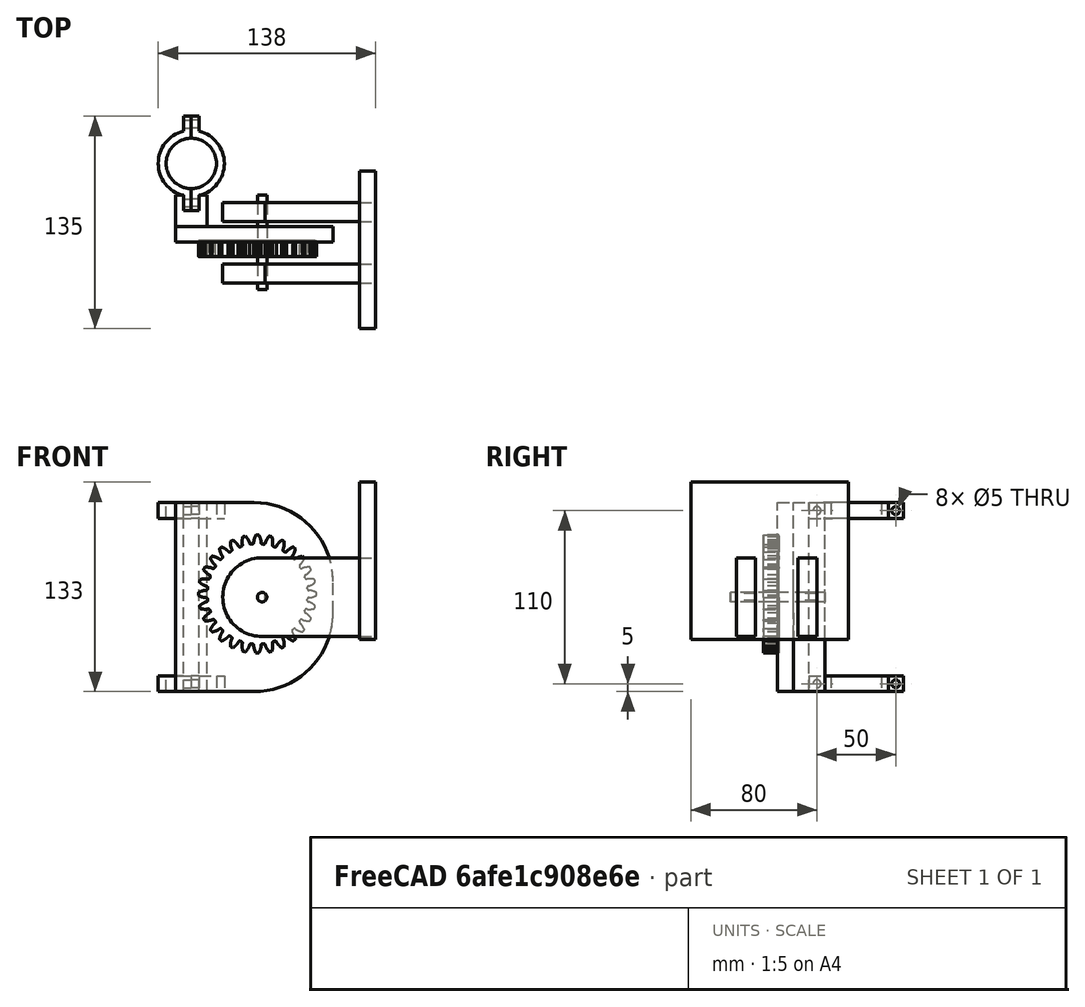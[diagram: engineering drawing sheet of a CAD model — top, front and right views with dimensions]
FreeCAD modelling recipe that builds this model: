
FCSTD DOCUMENT  (FreeCAD 0.18R4 (GitTag))
Label: Rotor_Z
License: All rights reserved
LicenseURL: http://en.wikipedia.org/wiki/All_rights_reserved
objects: Part::Cylinder×25, Part::Cut×19, Part::Box×14, Part::MultiFuse×6, Part::Fuse×4, Part::Fillet×2, Part::Part2DObjectPython×1, Part::Extrusion×1
note: 72 computed .brp shape members not serialized (recipe doc carries the construction recipe); baked Part::Feature solids carry a one-line shape summary decoded from their .brp

FEATURE [Part::Box] Box  label="Cubo"
  AttacherType = Attacher::AttachEngine3D
  Height = 10
  Length = 10
  Placement = pos=(-5,-30,0) rot=(0,0,1;0rad)
  Width = 60
FEATURE [Part::Box] Box001  label="Cubo001"
  AttacherType = Attacher::AttachEngine3D
  Height = 10
  Length = 21
  Placement = pos=(0,-30,0) rot=(0,0,1;0rad)
  Width = 60
FEATURE [Part::Cylinder] Cylinder  label="Cilindro"
  Angle = 360
  AttacherType = Attacher::AttachEngine3D
  Height = 10
  Placement = pos=(-5,-25,5) rot=(0,1,0;1.5708rad)
  Radius = 2.5
FEATURE [Part::Cylinder] Cylinder003  label="Cilindro001"
  Angle = 360
  AttacherType = Attacher::AttachEngine3D
  Height = 10
  Placement = pos=(-5,25,5) rot=(0,1,0;1.5708rad)
  Radius = 2.5
FEATURE [Part::MultiFuse] Fusion001  label="Agug"
  Shapes = -> [Cylinder,Cylinder003]
FEATURE [Part::Box] Box012  label="Cubo012"
  AttacherType = Attacher::AttachEngine3D
  Height = 120
  Length = 10
  Placement = pos=(-5,-45,0) rot=(0,0,1;0rad)
  Width = 10
FEATURE [Part::Box] Box013  label="Cubo013"
  AttacherType = Attacher::AttachEngine3D
  Height = 120
  Length = 20
  Placement = pos=(-10,-55,0) rot=(0,0,1;0rad)
  Width = 20
FEATURE [Part::Box] Box014  label="Cubo014"
  AttacherType = Attacher::AttachEngine3D
  Height = 120
  Length = 100
  Placement = pos=(-10,-46,0) rot=(0,0,1;0rad)
  Width = 10
FEATURE [Part::Part2DObjectPython] InvoluteGear  # Draft 2D object (typed FeaturePython)
  ExternalGear = true
  HighPrecision = true
  Modules = 2.5
  NumberOfTeeth = 28
  PressureAngle = 20
FEATURE [Part::Extrusion] Extrude
  Base = -> InvoluteGear
  Dir = (0,0,1)
  DirMode = 2
  FaceMakerClass = Part::FaceMakerBullseye
  LengthFwd = 10
  LengthRev = 0
  Placement = pos=(42,-45,62) rot=(1,0,0;1.5708rad)
  Solid = true
  Symmetric = false
FEATURE [Part::Box] Box015  label="Cubo015"
  AttacherType = Attacher::AttachEngine3D
  Height = 12
  Length = 70
  Placement = pos=(31,-70,-13) rot=(0,0,1;0rad)
  Width = 50
FEATURE [Part::Cylinder] Cylinder016  label="Cilindro008"
  Angle = 360
  AttacherType = Attacher::AttachEngine3D
  Height = 12
  Placement = pos=(29,-45,-13) rot=(0,0,1;0rad)
  Radius = 25
FEATURE [Part::Cylinder] Cylinder017  label="Cilindro009"
  Angle = 360
  AttacherType = Attacher::AttachEngine3D
  Height = 12
  Placement = pos=(29,-45,-13) rot=(0,0,1;0rad)
  Radius = 3
FEATURE [Part::Cut] Cut017
  Base = -> Cylinder016
  Tool = -> Cylinder017
FEATURE [Part::MultiFuse] Fusion008  label="lateral"
  Placement = pos=(16,-34,105) rot=(1,0,0;1.5708rad)
  Shapes = -> [Box015,Cut017]
FEATURE [Part::Box] Box016  label="Cubo016"
  AttacherType = Attacher::AttachEngine3D
  Height = 12
  Length = 70
  Placement = pos=(31,-70,-13) rot=(0,0,1;0rad)
  Width = 50
FEATURE [Part::Cylinder] Cylinder018  label="Cilindro010"
  Angle = 360
  AttacherType = Attacher::AttachEngine3D
  Height = 12
  Placement = pos=(29,-45,-13) rot=(0,0,1;0rad)
  Radius = 25
FEATURE [Part::Cylinder] Cylinder019  label="Cilindro011"
  Angle = 360
  AttacherType = Attacher::AttachEngine3D
  Height = 12
  Placement = pos=(29,-45,-13) rot=(0,0,1;0rad)
  Radius = 3
FEATURE [Part::Cut] Cut018
  Base = -> Cylinder018
  Tool = -> Cylinder019
FEATURE [Part::MultiFuse] Fusion009  label="lateral001"
  Placement = pos=(16,-73,105) rot=(1,0,0;1.5708rad)
  Shapes = -> [Box016,Cut018]
FEATURE [Part::Box] Box017  label="Cubo017"
  AttacherType = Attacher::AttachEngine3D
  Height = 100
  Length = 10
  Placement = pos=(107,-101,33) rot=(0,0,1;0rad)
  Width = 100
FEATURE [Part::Cylinder] Cylinder020  label="Cilindro012"
  Angle = 360
  AttacherType = Attacher::AttachEngine3D
  Height = 60
  Placement = pos=(45,-16,60) rot=(1,0,0;1.5708rad)
  Radius = 3
FEATURE [Part::Fillet] Fillet
  Base = -> Box014
  Edges = 1 edges r=50: [Edge8]
FEATURE [Part::Fillet] Fillet001
  Base = -> Fillet
  Edges = 1 edges r=50: [Edge3]
FEATURE [Part::Cylinder] Cylinder021  label="Cilindro 32"
  Angle = 360
  AttacherType = Attacher::AttachEngine3D
  Height = 10
  Radius = 16
FEATURE [Part::Cylinder] Cylinder022  label="Cilindro42"
  Angle = 360
  AttacherType = Attacher::AttachEngine3D
  Height = 10
  Radius = 21
FEATURE [Part::Cut] Cut019
  Base = -> Cylinder022
  Tool = -> Cylinder021
FEATURE [Part::Fuse] Fusion
  Base = -> Box
  Tool = -> Cut019
FEATURE [Part::Cut] Cut
  Base = -> Fusion
  Tool = -> Fusion001
FEATURE [Part::Cut] Cut020
  Base = -> Cut
  Tool = -> Box001
FEATURE [Part::Cylinder] Cylinder023  label="Cilindro013"
  Angle = 360
  AttacherType = Attacher::AttachEngine3D
  Height = 10
  Radius = 16
FEATURE [Part::Cut] Cut021  label="Brida"
  Base = -> Cut020
  Placement = pos=(0,4,10) rot=(0,1,0;3.14159rad)
  Tool = -> Cylinder023
FEATURE [Part::Cylinder] Cylinder024  label="Cilindro014"
  Angle = 360
  AttacherType = Attacher::AttachEngine3D
  Height = 10
  Placement = pos=(-5,25,5) rot=(0,1,0;1.5708rad)
  Radius = 2.5
FEATURE [Part::Box] Box018  label="Cubo018"
  AttacherType = Attacher::AttachEngine3D
  Height = 10
  Length = 10
  Placement = pos=(-5,-30,0) rot=(0,0,1;0rad)
  Width = 60
FEATURE [Part::Cylinder] Cylinder025  label="Cilindro015"
  Angle = 360
  AttacherType = Attacher::AttachEngine3D
  Height = 10
  Placement = pos=(-5,-25,5) rot=(0,1,0;1.5708rad)
  Radius = 2.5
FEATURE [Part::Box] Box019  label="Cubo019"
  AttacherType = Attacher::AttachEngine3D
  Height = 10
  Length = 21
  Placement = pos=(0,-30,0) rot=(0,0,1;0rad)
  Width = 60
FEATURE [Part::MultiFuse] Fusion010  label="Agug001"
  Shapes = -> [Cylinder025,Cylinder024]
FEATURE [Part::Cylinder] Cylinder026  label="Cilindro 033"
  Angle = 360
  AttacherType = Attacher::AttachEngine3D
  Height = 10
  Radius = 16
FEATURE [Part::Cylinder] Cylinder027  label="Cilindro016"
  Angle = 360
  AttacherType = Attacher::AttachEngine3D
  Height = 10
  Radius = 21
FEATURE [Part::Cut] Cut024
  Base = -> Cylinder027
  Tool = -> Cylinder026
FEATURE [Part::Fuse] Fusion011
  Base = -> Box018
  Tool = -> Cut024
FEATURE [Part::Cut] Cut025
  Base = -> Fusion011
  Tool = -> Fusion010
FEATURE [Part::Cut] Cut022
  Base = -> Cut025
  Tool = -> Box019
FEATURE [Part::Cylinder] Cylinder028  label="Cilindro017"
  Angle = 360
  AttacherType = Attacher::AttachEngine3D
  Height = 10
  Radius = 16
FEATURE [Part::Cut] Cut023  label="Brida001"
  Base = -> Cut022
  Placement = pos=(0,4,0) rot=(0,0,1;0rad)
  Tool = -> Cylinder028
FEATURE [Part::Cylinder] Cylinder029  label="Cilindro018"
  Angle = 360
  AttacherType = Attacher::AttachEngine3D
  Height = 10
  Placement = pos=(-5,25,5) rot=(0,1,0;1.5708rad)
  Radius = 2.5
FEATURE [Part::Box] Box020  label="Cubo020"
  AttacherType = Attacher::AttachEngine3D
  Height = 10
  Length = 10
  Placement = pos=(-5,-30,0) rot=(0,0,1;0rad)
  Width = 60
FEATURE [Part::Cylinder] Cylinder030  label="Cilindro019"
  Angle = 360
  AttacherType = Attacher::AttachEngine3D
  Height = 10
  Placement = pos=(-5,-25,5) rot=(0,1,0;1.5708rad)
  Radius = 2.5
FEATURE [Part::Box] Box021  label="Cubo021"
  AttacherType = Attacher::AttachEngine3D
  Height = 10
  Length = 21
  Placement = pos=(0,-30,0) rot=(0,0,1;0rad)
  Width = 60
FEATURE [Part::MultiFuse] Fusion012  label="Agug002"
  Shapes = -> [Cylinder030,Cylinder029]
FEATURE [Part::Cylinder] Cylinder031  label="Cilindro 034"
  Angle = 360
  AttacherType = Attacher::AttachEngine3D
  Height = 10
  Radius = 16
FEATURE [Part::Cylinder] Cylinder032  label="Cilindro020"
  Angle = 360
  AttacherType = Attacher::AttachEngine3D
  Height = 10
  Radius = 21
FEATURE [Part::Cut] Cut028
  Base = -> Cylinder032
  Tool = -> Cylinder031
FEATURE [Part::Fuse] Fusion013
  Base = -> Box020
  Tool = -> Cut028
FEATURE [Part::Cut] Cut029
  Base = -> Fusion013
  Tool = -> Fusion012
FEATURE [Part::Cut] Cut026
  Base = -> Cut029
  Tool = -> Box021
FEATURE [Part::Cylinder] Cylinder033  label="Cilindro021"
  Angle = 360
  AttacherType = Attacher::AttachEngine3D
  Height = 10
  Radius = 16
FEATURE [Part::Cut] Cut027  label="Brida002"
  Base = -> Cut026
  Placement = pos=(0,4,120) rot=(0,1,0;3.14159rad)
  Tool = -> Cylinder033
FEATURE [Part::Cylinder] Cylinder034  label="Cilindro022"
  Angle = 360
  AttacherType = Attacher::AttachEngine3D
  Height = 10
  Radius = 21
FEATURE [Part::Cylinder] Cylinder035  label="Cilindro023"
  Angle = 360
  AttacherType = Attacher::AttachEngine3D
  Height = 10
  Placement = pos=(-5,25,5) rot=(0,1,0;1.5708rad)
  Radius = 2.5
FEATURE [Part::Cylinder] Cylinder036  label="Cilindro024"
  Angle = 360
  AttacherType = Attacher::AttachEngine3D
  Height = 10
  Placement = pos=(-5,-25,5) rot=(0,1,0;1.5708rad)
  Radius = 2.5
FEATURE [Part::MultiFuse] Fusion014  label="Agug003"
  Shapes = -> [Cylinder036,Cylinder035]
FEATURE [Part::Box] Box022  label="Cubo022"
  AttacherType = Attacher::AttachEngine3D
  Height = 10
  Length = 10
  Placement = pos=(-5,-30,0) rot=(0,0,1;0rad)
  Width = 60
FEATURE [Part::Cylinder] Cylinder037  label="Cilindro 035"
  Angle = 360
  AttacherType = Attacher::AttachEngine3D
  Height = 10
  Radius = 16
FEATURE [Part::Cut] Cut033
  Base = -> Cylinder034
  Tool = -> Cylinder037
FEATURE [Part::Fuse] Fusion015
  Base = -> Box022
  Tool = -> Cut033
FEATURE [Part::Cut] Cut032
  Base = -> Fusion015
  Tool = -> Fusion014
FEATURE [Part::Box] Box023  label="Cubo023"
  AttacherType = Attacher::AttachEngine3D
  Height = 10
  Length = 21
  Placement = pos=(0,-30,0) rot=(0,0,1;0rad)
  Width = 60
FEATURE [Part::Cut] Cut030
  Base = -> Cut032
  Tool = -> Box023
FEATURE [Part::Cylinder] Cylinder038  label="Cilindro025"
  Angle = 360
  AttacherType = Attacher::AttachEngine3D
  Height = 10
  Radius = 16
FEATURE [Part::Cut] Cut031  label="Brida003"
  Base = -> Cut030
  Placement = pos=(0,4,110) rot=(0,0,1;0rad)
  Tool = -> Cylinder038
FEATURE [Part::Cut] Cut034
  Base = -> Box013
  Placement = pos=(0,19,0) rot=(0,0,1;0rad)
  Tool = -> Box012
